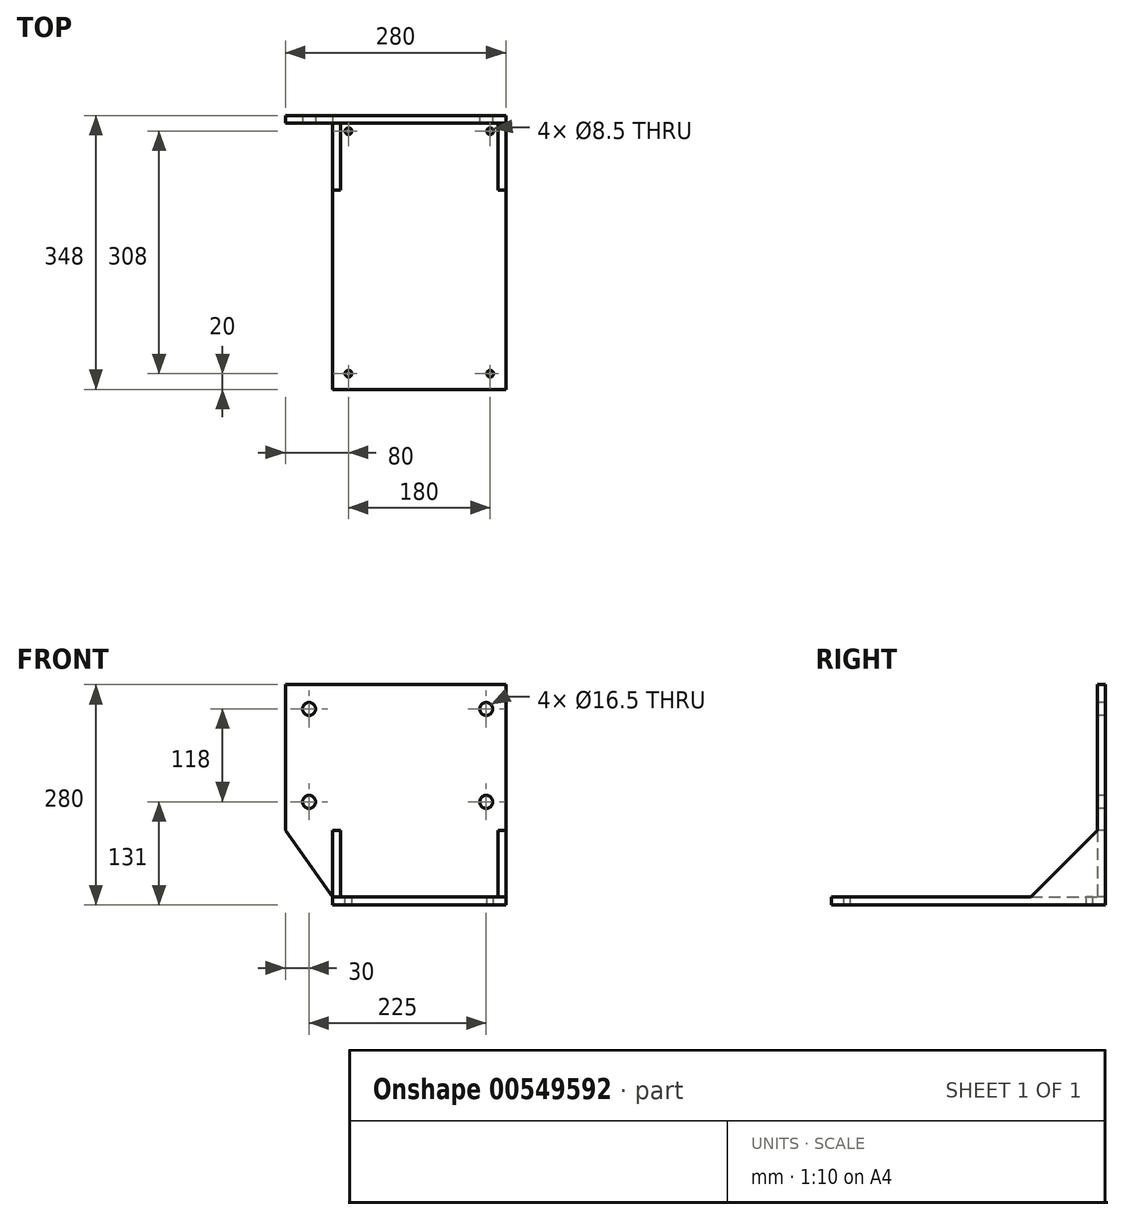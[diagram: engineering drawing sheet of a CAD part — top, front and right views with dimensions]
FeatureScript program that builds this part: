
annotation { "Feature Type Name" : "Feature", "Feature Type Description" : "" }
export const myFeature = defineFeature(function(context is Context, id is Id, definition is map)
    precondition{}
    {
        {
            var Q0;
            Q0=qCreatedBy(makeId("Right.planeOp"),FACE);
            var sketch = newSketch(context, id + "F0", { "sketchPlane" : qUnion([Q0])});
            skLineSegment(sketch, "E0", {"start": v(10, 135) * mm, "end": v(10, -145) * mm});
            skLineSegment(sketch, "E1", {"start": v(10, -145) * mm, "end": v(-338, -145) * mm});
            skLineSegment(sketch, "E2", {"start": v(-338, -145) * mm, "end": v(-338, -135) * mm});
            skLineSegment(sketch, "E3", {"start": v(-338, -135) * mm, "end": v(0, -135) * mm});
            skLineSegment(sketch, "E4", {"start": v(0, -135) * mm, "end": v(0, 135) * mm});
            skLineSegment(sketch, "E5", {"start": v(0, 135) * mm, "end": v(10, 135) * mm});
            skSolve(sketch);
        }
        {
            var Q0;
            Q0=makeQuery(id+"F0.imprint","IMPRINT",FACE,{"disambiguationData":[TD([[makeQuery(id+"F0.imprint","IMPRINT",EDGE,{"derivedFrom":sQuery(id+"F0.wireOp",EDGE,"E0")}),-1.0]])]});
            extrude(context, id + "F1", {"entities" : qUnion([Q0]), "depth" : 280 * mm, "offsetDistance" : 25 * mm});
        }
        {
            var Q0;
            Q0=makeQuery(id+"F1.opExtrude","SWEPT_FACE",FACE,{"disambiguationData":[OSD([sQuery(id+"F0.wireOp",EDGE,"E3")])]});
            var sketch = newSketch(context, id + "F2", { "sketchPlane" : qUnion([Q0])});
            skLineSegment(sketch, "E6.bottom", {"start": v(0, 0) * mm, "end": v(60, 0) * mm});
            skLineSegment(sketch, "E6.top", {"start": v(0, -338) * mm, "end": v(60, -338) * mm});
            skLineSegment(sketch, "E6.left", {"start": v(0, 0) * mm, "end": v(0, -338) * mm});
            skLineSegment(sketch, "E6.right", {"start": v(60, 0) * mm, "end": v(60, -338) * mm});
            skSolve(sketch);
        }
        {
            var Q0;
            Q0=makeQuery(id+"F2.imprint","IMPRINT",FACE,{"disambiguationData":[TD([[makeQuery(id+"F2.imprint","IMPRINT",EDGE,{"derivedFrom":sQuery(id+"F2.wireOp",EDGE,"E6.bottom")}),1.0]])]});
            extrude(context, id + "F3", {"entities" : qUnion([Q0]), "operationType" : NewBodyOperationType.REMOVE, "endBound" : BoundingType.THROUGH_ALL, "oppositeDirection" : true, "depth" : 25 * mm, "offsetDistance" : 25 * mm});
        }
        {
            var Q0;
            Q0=makeQuery(id+"F3.boolean.opBoolean","MERGE",FACE,{"derivedFrom":[makeQuery(id+"F1.opExtrude","SWEPT_FACE",FACE,{"disambiguationData":[OSD([sQuery(id+"F0.wireOp",EDGE,"E4")])]}),makeQuery(id+"F3.opExtrude","SWEPT_FACE",FACE,{"disambiguationData":[OSD([sQuery(id+"F2.wireOp",EDGE,"E6.bottom")])]})]});
            var sketch = newSketch(context, id + "F4", { "sketchPlane" : qUnion([Q0])});
            skLineSegment(sketch, "E7", {"start": v(-171.67, -50) * mm, "end": v(440.13, -50) * mm, "construction": true});
            skLineSegment(sketch, "E8", {"start": v(0, -50) * mm, "end": v(60, -135) * mm});
            skSolve(sketch);
        }
        {
            var Q0;
            {var subQ0=sQuery(id+"F4.wireOp",EDGE,"E8");Q0=makeQuery(id+"F4.imprint","IMPRINT",FACE,{"disambiguationData":[TD([[makeQuery(id+"F4.imprint","IMPRINT",EDGE,{"derivedFrom":subQ0}),-1.0]])]});}
            extrude(context, id + "F5", {"entities" : qUnion([Q0]), "operationType" : NewBodyOperationType.REMOVE, "endBound" : BoundingType.THROUGH_ALL, "oppositeDirection" : true, "depth" : 25 * mm, "offsetDistance" : 25 * mm});
        }
        {
            var Q0;
            Q0=makeQuery(id+"F3.boolean.opBoolean","MERGE",FACE,{"derivedFrom":[makeQuery(id+"F1.opExtrude","SWEPT_FACE",FACE,{"disambiguationData":[OSD([sQuery(id+"F0.wireOp",EDGE,"E4")])]}),makeQuery(id+"F3.opExtrude","SWEPT_FACE",FACE,{"disambiguationData":[OSD([sQuery(id+"F2.wireOp",EDGE,"E6.bottom")])]})]});
            var sketch = newSketch(context, id + "F6", { "sketchPlane" : qUnion([Q0])});
            skLineSegment(sketch, "E9", {"start": v(-102.39, 104) * mm, "end": v(372, 104) * mm, "construction": true});
            skLineSegment(sketch, "E10", {"start": v(255, 175.14) * mm, "end": v(255, -108.87) * mm, "construction": true});
            skLineSegment(sketch, "E11", {"start": v(30, 197.94) * mm, "end": v(30, -102.46) * mm, "construction": true});
            skLineSegment(sketch, "E12", {"start": v(-48.37, -14) * mm, "end": v(380.67, -14) * mm, "construction": true});
            skCircle(sketch, "E13", {"center": v(255, 104) * mm, "radius": 8.25 * mm});
            skCircle(sketch, "E14", {"center": v(30, 104) * mm, "radius": 8.25 * mm});
            skCircle(sketch, "E15", {"center": v(30, -14) * mm, "radius": 8.25 * mm});
            skCircle(sketch, "E16", {"center": v(255, -14) * mm, "radius": 8.25 * mm});
            skSolve(sketch);
        }
        {
            var Q0;
            Q0=makeQuery(id+"F6.imprint","IMPRINT",FACE,{"disambiguationData":[TD([[makeQuery(id+"F6.imprint","IMPRINT",EDGE,{"derivedFrom":sQuery(id+"F6.wireOp",EDGE,"E14")}),1.0]])]});
            var Q1;
            Q1=makeQuery(id+"F6.imprint","IMPRINT",FACE,{"disambiguationData":[TD([[makeQuery(id+"F6.imprint","IMPRINT",EDGE,{"derivedFrom":sQuery(id+"F6.wireOp",EDGE,"E13")}),1.0]])]});
            var Q2;
            Q2=makeQuery(id+"F6.imprint","IMPRINT",FACE,{"disambiguationData":[TD([[makeQuery(id+"F6.imprint","IMPRINT",EDGE,{"derivedFrom":sQuery(id+"F6.wireOp",EDGE,"E16")}),1.0]])]});
            var Q3;
            Q3=makeQuery(id+"F6.imprint","IMPRINT",FACE,{"disambiguationData":[TD([[makeQuery(id+"F6.imprint","IMPRINT",EDGE,{"derivedFrom":sQuery(id+"F6.wireOp",EDGE,"E15")}),1.0]])]});
            extrude(context, id + "F7", {"entities" : qUnion([Q0, Q1, Q2, Q3]), "operationType" : NewBodyOperationType.REMOVE, "endBound" : BoundingType.THROUGH_ALL, "oppositeDirection" : true, "depth" : 25 * mm, "offsetDistance" : 25 * mm});
        }
        {
            var Q0;
            Q0=makeQuery(id+"F1.opExtrude","SWEPT_FACE",FACE,{"disambiguationData":[OSD([sQuery(id+"F0.wireOp",EDGE,"E3")])]});
            var sketch = newSketch(context, id + "F8", { "sketchPlane" : qUnion([Q0])});
            skLineSegment(sketch, "E17", {"start": v(0, -318) * mm, "end": v(316.15, -318) * mm, "construction": true});
            skLineSegment(sketch, "E18", {"start": v(0, -10) * mm, "end": v(324.4, -10) * mm, "construction": true});
            skLineSegment(sketch, "E19", {"start": v(260, -5.15) * mm, "end": v(260, -328.96) * mm, "construction": true});
            skLineSegment(sketch, "E20", {"start": v(80, -4.52) * mm, "end": v(80, -329.6) * mm, "construction": true});
            skCircle(sketch, "E21", {"center": v(80, -10) * mm, "radius": 4.25 * mm});
            skCircle(sketch, "E22", {"center": v(80, -318) * mm, "radius": 4.25 * mm});
            skCircle(sketch, "E23", {"center": v(260, -10) * mm, "radius": 4.25 * mm});
            skCircle(sketch, "E24", {"center": v(260, -318) * mm, "radius": 4.25 * mm});
            skSolve(sketch);
        }
        {
            var Q0;
            Q0=makeQuery(id+"F8.imprint","IMPRINT",FACE,{"disambiguationData":[TD([[makeQuery(id+"F8.imprint","IMPRINT",EDGE,{"derivedFrom":sQuery(id+"F8.wireOp",EDGE,"E21")}),1.0]])]});
            var Q1;
            Q1=makeQuery(id+"F8.imprint","IMPRINT",FACE,{"disambiguationData":[TD([[makeQuery(id+"F8.imprint","IMPRINT",EDGE,{"derivedFrom":sQuery(id+"F8.wireOp",EDGE,"E23")}),1.0]])]});
            var Q2;
            Q2=makeQuery(id+"F8.imprint","IMPRINT",FACE,{"disambiguationData":[TD([[makeQuery(id+"F8.imprint","IMPRINT",EDGE,{"derivedFrom":sQuery(id+"F8.wireOp",EDGE,"E22")}),1.0]])]});
            var Q3;
            Q3=makeQuery(id+"F8.imprint","IMPRINT",FACE,{"disambiguationData":[TD([[makeQuery(id+"F8.imprint","IMPRINT",EDGE,{"derivedFrom":sQuery(id+"F8.wireOp",EDGE,"E24")}),1.0]])]});
            extrude(context, id + "F9", {"entities" : qUnion([Q0, Q1, Q2, Q3]), "operationType" : NewBodyOperationType.REMOVE, "endBound" : BoundingType.THROUGH_ALL, "oppositeDirection" : true, "depth" : 25 * mm, "offsetDistance" : 25 * mm});
        }
        {
            var Q0;
            Q0=makeQuery(id+"F3.boolean.opBoolean","MERGE",FACE,{"derivedFrom":[makeQuery(id+"F1.opExtrude","SWEPT_FACE",FACE,{"disambiguationData":[OSD([sQuery(id+"F0.wireOp",EDGE,"E4")])]}),makeQuery(id+"F3.opExtrude","SWEPT_FACE",FACE,{"disambiguationData":[OSD([sQuery(id+"F2.wireOp",EDGE,"E6.bottom")])]})]});
            var sketch = newSketch(context, id + "F10", { "sketchPlane" : qUnion([Q0])});
            skLineSegment(sketch, "E25.bottom", {"start": v(280, -50) * mm, "end": v(270, -50) * mm});
            skLineSegment(sketch, "E25.top", {"start": v(280, -135) * mm, "end": v(270, -135) * mm});
            skLineSegment(sketch, "E25.left", {"start": v(280, -50) * mm, "end": v(280, -135) * mm});
            skLineSegment(sketch, "E25.right", {"start": v(270, -50) * mm, "end": v(270, -135) * mm});
            skLineSegment(sketch, "E26.bottom", {"start": v(60, -135) * mm, "end": v(70, -135) * mm});
            skLineSegment(sketch, "E26.top", {"start": v(60, -50) * mm, "end": v(70, -50) * mm});
            skLineSegment(sketch, "E26.left", {"start": v(60, -135) * mm, "end": v(60, -50) * mm});
            skLineSegment(sketch, "E26.right", {"start": v(70, -135) * mm, "end": v(70, -50) * mm});
            skSolve(sketch);
        }
        {
            var Q0;
            Q0=makeQuery(id+"F10.imprint","IMPRINT",FACE,{"disambiguationData":[TD([[makeQuery(id+"F10.imprint","IMPRINT",EDGE,{"derivedFrom":sQuery(id+"F10.wireOp",EDGE,"E26.bottom")}),-1.0]])]});
            var Q1;
            Q1=makeQuery(id+"F10.imprint","IMPRINT",FACE,{"disambiguationData":[TD([[makeQuery(id+"F10.imprint","IMPRINT",EDGE,{"derivedFrom":sQuery(id+"F10.wireOp",EDGE,"E25.bottom")}),1.0]])]});
            extrude(context, id + "F11", {"entities" : qUnion([Q0, Q1]), "operationType" : NewBodyOperationType.ADD, "depth" : 85 * mm, "offsetDistance" : 25 * mm});
        }
        {
            var Q0;
            Q0=makeQuery(id+"F11.boolean.opBoolean","MERGE",FACE,{"derivedFrom":[makeQuery(id+"F1.opExtrude","CAP_FACE",FACE,{"disambiguationData":[OSD([sQuery(id+"F0.wireOp",EDGE,"E0"),sQuery(id+"F0.wireOp",EDGE,"E1"),sQuery(id+"F0.wireOp",EDGE,"E2"),sQuery(id+"F0.wireOp",EDGE,"E3"),sQuery(id+"F0.wireOp",EDGE,"E4"),sQuery(id+"F0.wireOp",EDGE,"E5")])],"isStart":false}),makeQuery(id+"F11.opExtrude","SWEPT_FACE",FACE,{"disambiguationData":[OSD([sQuery(id+"F10.wireOp",EDGE,"E25.left")])]})]});
            var sketch = newSketch(context, id + "F12", { "sketchPlane" : qUnion([Q0])});
            skLineSegment(sketch, "E27", {"start": v(0, -50) * mm, "end": v(-85, -135) * mm});
            skSolve(sketch);
        }
        {
            var Q0;
            {var subQ0=sQuery(id+"F2.wireOp",EDGE,"E6.right");Q0=makeQuery(id+"F11.boolean.opBoolean","MERGE",FACE,{"derivedFrom":[makeQuery(id+"F5.boolean.opBoolean","MERGE",FACE,{"derivedFrom":[makeQuery(id+"F3.boolean.opBoolean","COPY",FACE,{"derivedFrom":makeQuery(id+"F3.opExtrude","SWEPT_FACE",FACE,{"disambiguationData":[OSD([subQ0])]})}),makeQuery(id+"F5.opExtrude","SWEPT_FACE",FACE,{"disambiguationData":[OSD([sQuery(id+"F0.wireOp",EDGE,"E3"),sQuery(id+"F0.wireOp",EDGE,"E4"),sQuery(id+"F2.wireOp",EDGE,"E6.bottom"),subQ0])]})]}),makeQuery(id+"F11.opExtrude","SWEPT_FACE",FACE,{"disambiguationData":[OSD([sQuery(id+"F10.wireOp",EDGE,"E26.left")])]})]});}
            var sketch = newSketch(context, id + "F13", { "sketchPlane" : qUnion([Q0])});
            skLineSegment(sketch, "E28", {"start": v(0, -50) * mm, "end": v(85, -135) * mm});
            skSolve(sketch);
        }
        {
            var Q0;
            Q0=makeQuery(id+"F13.imprint","IMPRINT",FACE,{"disambiguationData":[TD([[makeQuery(id+"F13.imprint","IMPRINT",EDGE,{"derivedFrom":sQuery(id+"F13.wireOp",EDGE,"E28")}),1.0]])]});
            extrude(context, id + "F14", {"entities" : qUnion([Q0]), "operationType" : NewBodyOperationType.REMOVE, "endBound" : BoundingType.THROUGH_ALL, "oppositeDirection" : true, "depth" : 25 * mm, "offsetDistance" : 25 * mm});
        }
        {
            var Q0;
            Q0=makeQuery(id+"F12.imprint","IMPRINT",FACE,{"disambiguationData":[TD([[makeQuery(id+"F12.imprint","IMPRINT",EDGE,{"derivedFrom":sQuery(id+"F12.wireOp",EDGE,"E27")}),-1.0]])]});
            extrude(context, id + "F15", {"entities" : qUnion([Q0]), "operationType" : NewBodyOperationType.REMOVE, "endBound" : BoundingType.THROUGH_ALL, "oppositeDirection" : true, "depth" : 25 * mm, "offsetDistance" : 25 * mm});
        }
    });
